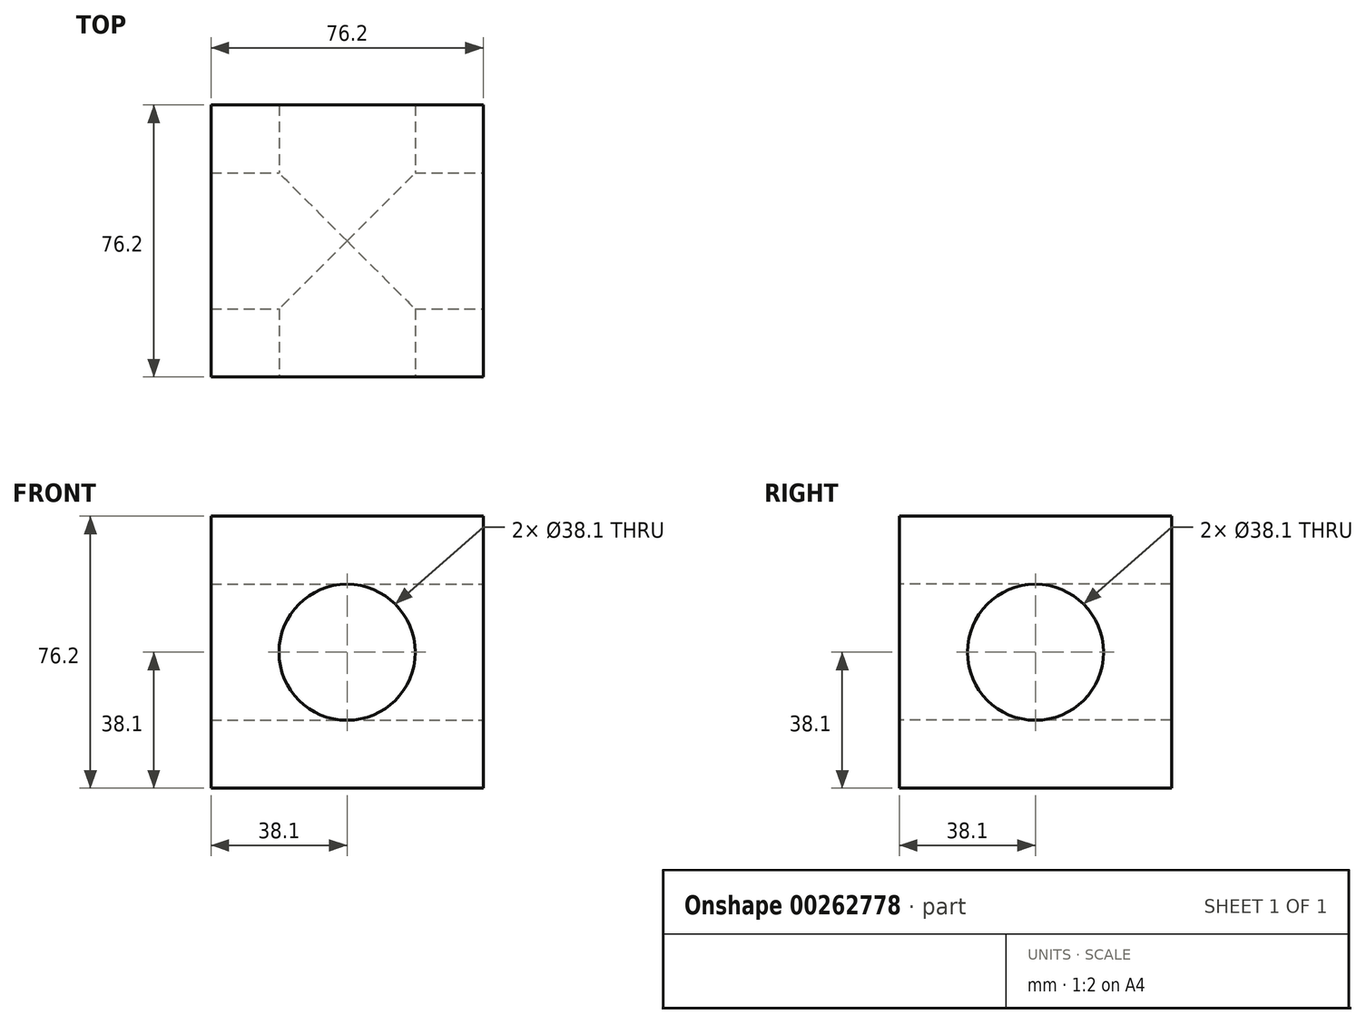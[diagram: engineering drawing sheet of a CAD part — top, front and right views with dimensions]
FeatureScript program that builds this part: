
annotation { "Feature Type Name" : "Feature", "Feature Type Description" : "" }
export const myFeature = defineFeature(function(context is Context, id is Id, definition is map)
    precondition{}
    {
        {
            var Q0;
            Q0=qCreatedBy(makeId("Front.planeOp"),FACE);
            var sketch = newSketch(context, id + "F0", { "sketchPlane" : qUnion([Q0])});
            skLineSegment(sketch, "E0.bottom", {"start": v(0, 0) * mm, "end": v(76.2, 0) * mm});
            skLineSegment(sketch, "E0.top", {"start": v(0, 76.2) * mm, "end": v(76.2, 76.2) * mm});
            skLineSegment(sketch, "E0.left", {"start": v(0, 0) * mm, "end": v(0, 76.2) * mm});
            skLineSegment(sketch, "E0.right", {"start": v(76.2, 0) * mm, "end": v(76.2, 76.2) * mm});
            skSolve(sketch);
        }
        {
            var Q0;
            Q0 = qSketchRegion(id + "F0", true);
            extrude(context, id + "F1", {"entities" : qUnion([Q0]), "depth" : 76.2 * mm});
        }
        {
            var Q0;
            Q0=makeQuery(id+"F1.opExtrude","SWEPT_FACE",FACE,{"disambiguationData":[OSD([sQuery(id+"F0.wireOp",EDGE,"E0.right")])]});
            var sketch = newSketch(context, id + "F2", { "sketchPlane" : qUnion([Q0])});
            skLineSegment(sketch, "E1", {"start": v(-76.2, 76.2) * mm, "end": v(0, 0) * mm, "construction": true});
            skCircle(sketch, "E2", {"center": v(-38.1, 38.1) * mm, "radius": 19.05 * mm});
            skSolve(sketch);
        }
        {
            var Q0;
            Q0 = qSketchRegion(id + "F2", true);
            extrude(context, id + "F3", {"entities" : qUnion([Q0]), "operationType" : NewBodyOperationType.REMOVE, "endBound" : BoundingType.THROUGH_ALL, "oppositeDirection" : true, "depth" : 25.4 * mm});
        }
        {
            var Q0;
            Q0=makeQuery(id+"F1.opExtrude","CAP_FACE",FACE,{"disambiguationData":[OSD([sQuery(id+"F0.wireOp",EDGE,"E0.bottom"),sQuery(id+"F0.wireOp",EDGE,"E0.top"),sQuery(id+"F0.wireOp",EDGE,"E0.left"),sQuery(id+"F0.wireOp",EDGE,"E0.right")])],"isStart":false});
            var sketch = newSketch(context, id + "F4", { "sketchPlane" : qUnion([Q0])});
            skLineSegment(sketch, "E3", {"start": v(0, 76.2) * mm, "end": v(76.2, 0) * mm, "construction": true});
            skCircle(sketch, "E4", {"center": v(38.1, 38.1) * mm, "radius": 19.05 * mm});
            skSolve(sketch);
        }
        {
            var Q0;
            Q0 = qSketchRegion(id + "F4", true);
            extrude(context, id + "F5", {"entities" : qUnion([Q0]), "operationType" : NewBodyOperationType.REMOVE, "oppositeDirection" : true, "depth" : 76.2 * mm});
        }
    });
